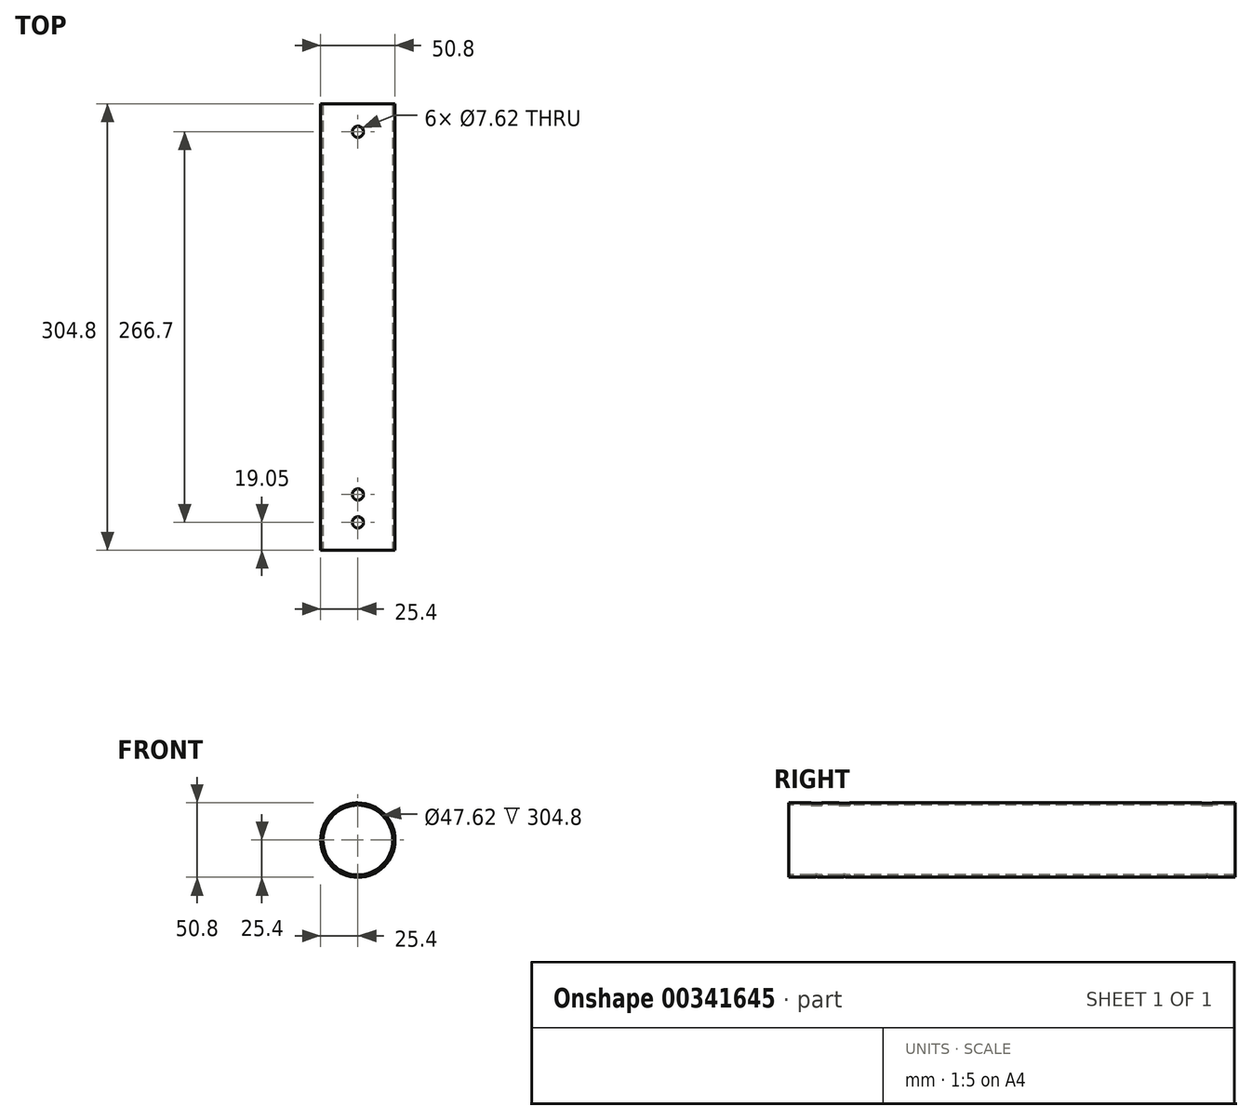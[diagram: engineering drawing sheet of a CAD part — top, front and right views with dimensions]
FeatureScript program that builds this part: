
annotation { "Feature Type Name" : "Feature", "Feature Type Description" : "" }
export const myFeature = defineFeature(function(context is Context, id is Id, definition is map)
    precondition{}
    {
        {
            var Q0;
            Q0=qCreatedBy(makeId("Front.planeOp"),FACE);
            var sketch = newSketch(context, id + "F0", { "sketchPlane" : qUnion([Q0])});
            skCircle(sketch, "E0", {"center": v(0, 0) * mm, "radius": 25.4 * mm});
            skCircle(sketch, "E1", {"center": v(0, 0) * mm, "radius": 23.81 * mm});
            skLineSegment(sketch, "E2", {"start": v(0, -25.4) * mm, "end": v(0, 25.4) * mm, "construction": true});
            skLineSegment(sketch, "E3", {"start": v(25.4, 0) * mm, "end": v(-25.4, 0) * mm, "construction": true});
            skSolve(sketch);
        }
        {
            var Q0;
            Q0=makeQuery(id+"F0.imprint","IMPRINT",FACE,{"disambiguationData":[TD([[makeQuery(id+"F0.imprint","IMPRINT",EDGE,{"derivedFrom":sQuery(id+"F0.wireOp",EDGE,"E0")}),1.0]])]});
            extrude(context, id + "F1", {"entities" : qUnion([Q0]), "oppositeDirection" : true, "depth" : 304.8 * mm});
        }
        {
            var Q0;
            Q0=qCreatedBy(makeId("Right.planeOp"),FACE);
            var sketch = newSketch(context, id + "F2", { "sketchPlane" : qUnion([Q0])});
            skLineSegment(sketch, "E4", {"start": v(152.4, -25.4) * mm, "end": v(0, -25.4) * mm});
            skLineSegment(sketch, "E5", {"start": v(304.8, -25.4) * mm, "end": v(0, -25.4) * mm});
            skLineSegment(sketch, "E6", {"start": v(0, 25.4) * mm, "end": v(304.8, 25.4) * mm});
            skSolve(sketch);
        }
        {
            var Q0;
            Q0=qCreatedBy(makeId("Top.planeOp"),FACE);
            var sketch = newSketch(context, id + "F3", { "sketchPlane" : qUnion([Q0])});
            skCircle(sketch, "E7", {"center": v(0, 19.05) * mm, "radius": 3.81 * mm});
            skCircle(sketch, "E8", {"center": v(0, 285.75) * mm, "radius": 3.81 * mm});
            skLineSegment(sketch, "E9", {"start": v(-25.4, 0) * mm, "end": v(-25.4, 304.8) * mm});
            skLineSegment(sketch, "E10", {"start": v(25.4, 304.8) * mm, "end": v(25.4, 0) * mm});
            skCircle(sketch, "E11", {"center": v(0, 38.1) * mm, "radius": 3.81 * mm});
            skSolve(sketch);
        }
        {
            var Q0;
            Q0 = qSketchRegion(id + "F3", true);
            extrude(context, id + "F4", {"entities" : qUnion([Q0]), "operationType" : NewBodyOperationType.REMOVE, "depth" : 25.4 * mm, "hasSecondDirection" : true, "secondDirectionOppositeDirection" : true, "secondDirectionDepth" : 25.4 * mm});
        }
    });
